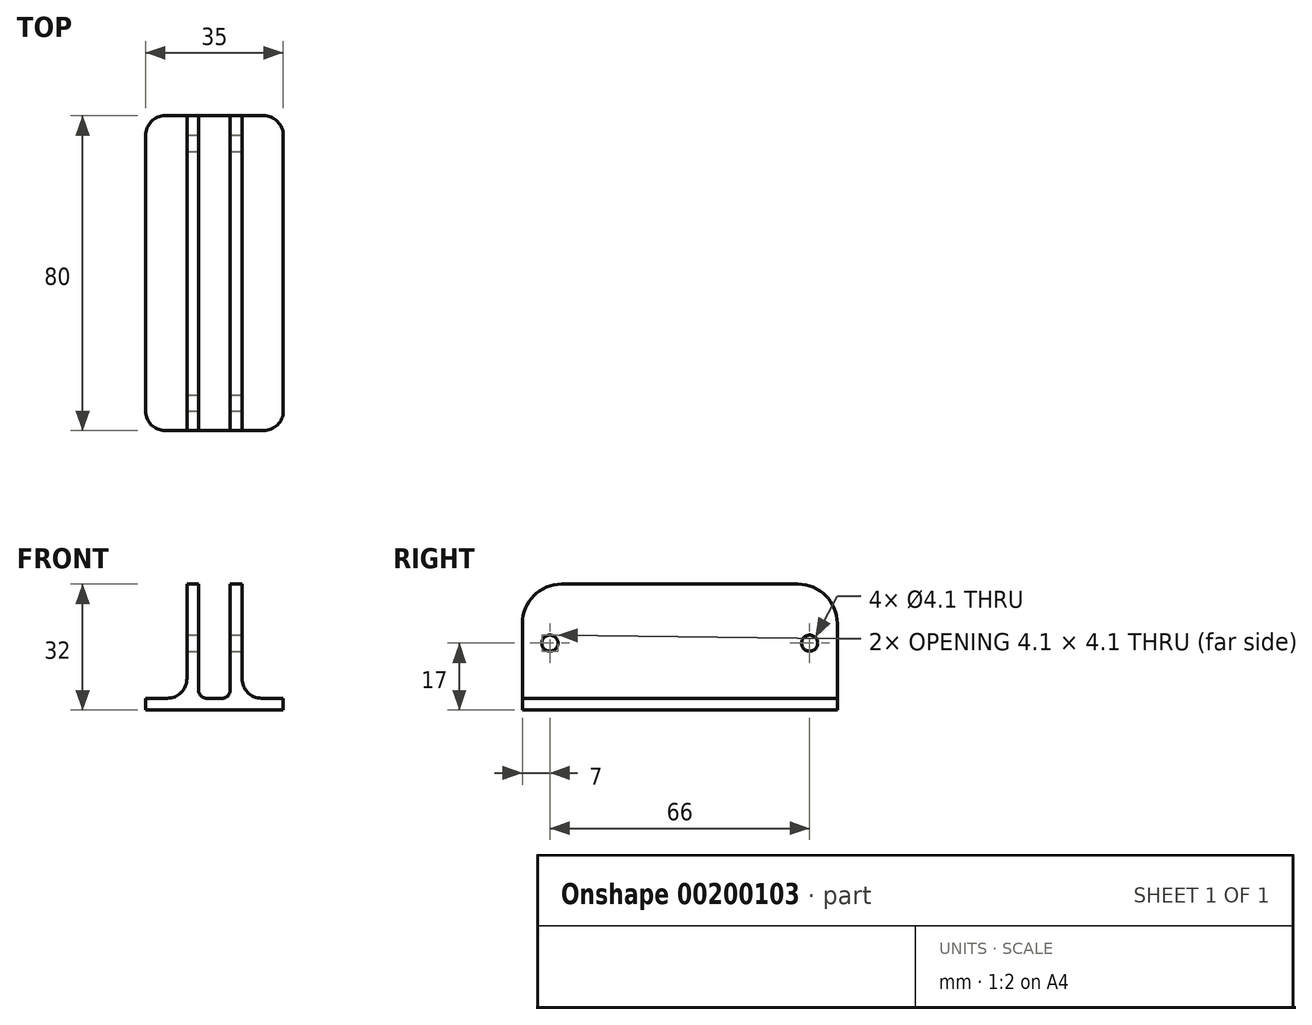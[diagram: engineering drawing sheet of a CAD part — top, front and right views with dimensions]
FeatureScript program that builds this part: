
annotation { "Feature Type Name" : "Feature", "Feature Type Description" : "" }
export const myFeature = defineFeature(function(context is Context, id is Id, definition is map)
    precondition{}
    {
        {
            var Q0;
            Q0=qCreatedBy(makeId("Front.planeOp"),FACE);
            var sketch = newSketch(context, id + "F0", { "sketchPlane" : qUnion([Q0])});
            skLineSegment(sketch, "E0", {"start": v(-17.5, 0) * mm, "end": v(-17.5, 3) * mm});
            skLineSegment(sketch, "E1", {"start": v(-17.5, 3) * mm, "end": v(-7, 3) * mm});
            skLineSegment(sketch, "E2", {"start": v(-7, 3) * mm, "end": v(-7, 32) * mm});
            skLineSegment(sketch, "E3", {"start": v(-7, 32) * mm, "end": v(-4, 32) * mm});
            skLineSegment(sketch, "E4", {"start": v(-4, 32) * mm, "end": v(-4, 3) * mm});
            skLineSegment(sketch, "E5", {"start": v(-4, 3) * mm, "end": v(4, 3) * mm});
            skLineSegment(sketch, "E6", {"start": v(4, 3) * mm, "end": v(4, 32) * mm});
            skLineSegment(sketch, "E7", {"start": v(4, 32) * mm, "end": v(7, 32) * mm});
            skLineSegment(sketch, "E8", {"start": v(7, 32) * mm, "end": v(7, 3) * mm});
            skLineSegment(sketch, "E9", {"start": v(7, 3) * mm, "end": v(17.5, 3) * mm});
            skLineSegment(sketch, "E10", {"start": v(17.5, 3) * mm, "end": v(17.5, 0) * mm});
            skLineSegment(sketch, "E11", {"start": v(17.5, 0) * mm, "end": v(-17.5, 0) * mm});
            skSolve(sketch);
        }
        {
            var Q0;
            Q0=makeQuery(id+"F0.imprint","IMPRINT",FACE,{"disambiguationData":[TD([[makeQuery(id+"F0.imprint","IMPRINT",EDGE,{"derivedFrom":sQuery(id+"F0.wireOp",EDGE,"E0")}),-1.0]])]});
            extrude(context, id + "F1", {"entities" : qUnion([Q0]), "endBound" : BoundingType.SYMMETRIC, "depth" : 80 * mm});
        }
        {
            var Q0;
            Q0=makeQuery(id+"F1.opExtrude","SWEPT_EDGE",EDGE,{"disambiguationData":[OSD([sQuery(id+"F0.wireOp",EDGE,"E4"),sQuery(id+"F0.wireOp",EDGE,"E5")])]});
            var Q1;
            Q1=makeQuery(id+"F1.opExtrude","SWEPT_EDGE",EDGE,{"disambiguationData":[OSD([sQuery(id+"F0.wireOp",EDGE,"E5"),sQuery(id+"F0.wireOp",EDGE,"E6")])]});
            fillet(context, id + "F2", {"entities" : qUnion([Q0, Q1]), "radius" : 2 * mm, "tangentPropagation" : true, "allowEdgeOverflow" : false});
        }
        {
            var Q0;
            Q0=makeQuery(id+"F1.opExtrude","CAP_EDGE",EDGE,{"disambiguationData":[OSD([sQuery(id+"F0.wireOp",EDGE,"E7")])],"isStart":true});
            var Q1;
            Q1=makeQuery(id+"F1.opExtrude","CAP_EDGE",EDGE,{"disambiguationData":[OSD([sQuery(id+"F0.wireOp",EDGE,"E3")])],"isStart":true});
            var Q2;
            Q2=makeQuery(id+"F1.opExtrude","CAP_EDGE",EDGE,{"disambiguationData":[OSD([sQuery(id+"F0.wireOp",EDGE,"E7")])],"isStart":false});
            var Q3;
            Q3=makeQuery(id+"F1.opExtrude","CAP_EDGE",EDGE,{"disambiguationData":[OSD([sQuery(id+"F0.wireOp",EDGE,"E3")])],"isStart":false});
            fillet(context, id + "F3", {"entities" : qUnion([Q0, Q1, Q2, Q3]), "radius" : 10 * mm, "tangentPropagation" : true, "allowEdgeOverflow" : false});
        }
        {
            var Q0;
            Q0=makeQuery(id+"F1.opExtrude","SWEPT_FACE",FACE,{"disambiguationData":[OSD([sQuery(id+"F0.wireOp",EDGE,"E8")])]});
            var sketch = newSketch(context, id + "F4", { "sketchPlane" : qUnion([Q0])});
            skCircle(sketch, "E12", {"center": v(-33, 17) * mm, "radius": 2.05 * mm});
            skCircle(sketch, "E13", {"center": v(33, 17) * mm, "radius": 2.05 * mm});
            skSolve(sketch);
        }
        {
            var Q0;
            Q0=makeQuery(id+"F4.imprint","IMPRINT",FACE,{"disambiguationData":[TD([[makeQuery(id+"F4.imprint","IMPRINT",EDGE,{"derivedFrom":sQuery(id+"F4.wireOp",EDGE,"E12")}),1.0]])]});
            var Q1;
            Q1=makeQuery(id+"F4.imprint","IMPRINT",FACE,{"disambiguationData":[TD([[makeQuery(id+"F4.imprint","IMPRINT",EDGE,{"derivedFrom":sQuery(id+"F4.wireOp",EDGE,"E13")}),1.0]])]});
            var Q2;
            Q2=makeQuery(id+"F1.opExtrude","SWEPT_FACE",FACE,{"disambiguationData":[OSD([sQuery(id+"F0.wireOp",EDGE,"E2")])]});
            extrude(context, id + "F5", {"entities" : qUnion([Q0, Q1]), "operationType" : NewBodyOperationType.REMOVE, "endBound" : BoundingType.UP_TO_SURFACE, "oppositeDirection" : true, "endBoundEntityFace" : qUnion([Q2]), "depth" : 25 * mm});
        }
        {
            var Q0;
            Q0=makeQuery(id+"F1.opExtrude","SWEPT_EDGE",EDGE,{"disambiguationData":[OSD([sQuery(id+"F0.wireOp",EDGE,"E8"),sQuery(id+"F0.wireOp",EDGE,"E9")])]});
            var Q1;
            Q1=makeQuery(id+"F1.opExtrude","SWEPT_EDGE",EDGE,{"disambiguationData":[OSD([sQuery(id+"F0.wireOp",EDGE,"E1"),sQuery(id+"F0.wireOp",EDGE,"E2")])]});
            fillet(context, id + "F6", {"entities" : qUnion([Q0, Q1]), "radius" : 5 * mm, "tangentPropagation" : true, "allowEdgeOverflow" : false});
        }
        {
            var Q0;
            Q0=makeQuery(id+"F1.opExtrude","CAP_EDGE",EDGE,{"disambiguationData":[OSD([sQuery(id+"F0.wireOp",EDGE,"E0")])],"isStart":false});
            var Q1;
            Q1=makeQuery(id+"F1.opExtrude","CAP_EDGE",EDGE,{"disambiguationData":[OSD([sQuery(id+"F0.wireOp",EDGE,"E10")])],"isStart":false});
            var Q2;
            Q2=makeQuery(id+"F1.opExtrude","CAP_EDGE",EDGE,{"disambiguationData":[OSD([sQuery(id+"F0.wireOp",EDGE,"E10")])],"isStart":true});
            var Q3;
            Q3=makeQuery(id+"F1.opExtrude","CAP_EDGE",EDGE,{"disambiguationData":[OSD([sQuery(id+"F0.wireOp",EDGE,"E0")])],"isStart":true});
            fillet(context, id + "F7", {"entities" : qUnion([Q0, Q1, Q2, Q3]), "radius" : 5 * mm, "tangentPropagation" : true, "allowEdgeOverflow" : false});
        }
    });
